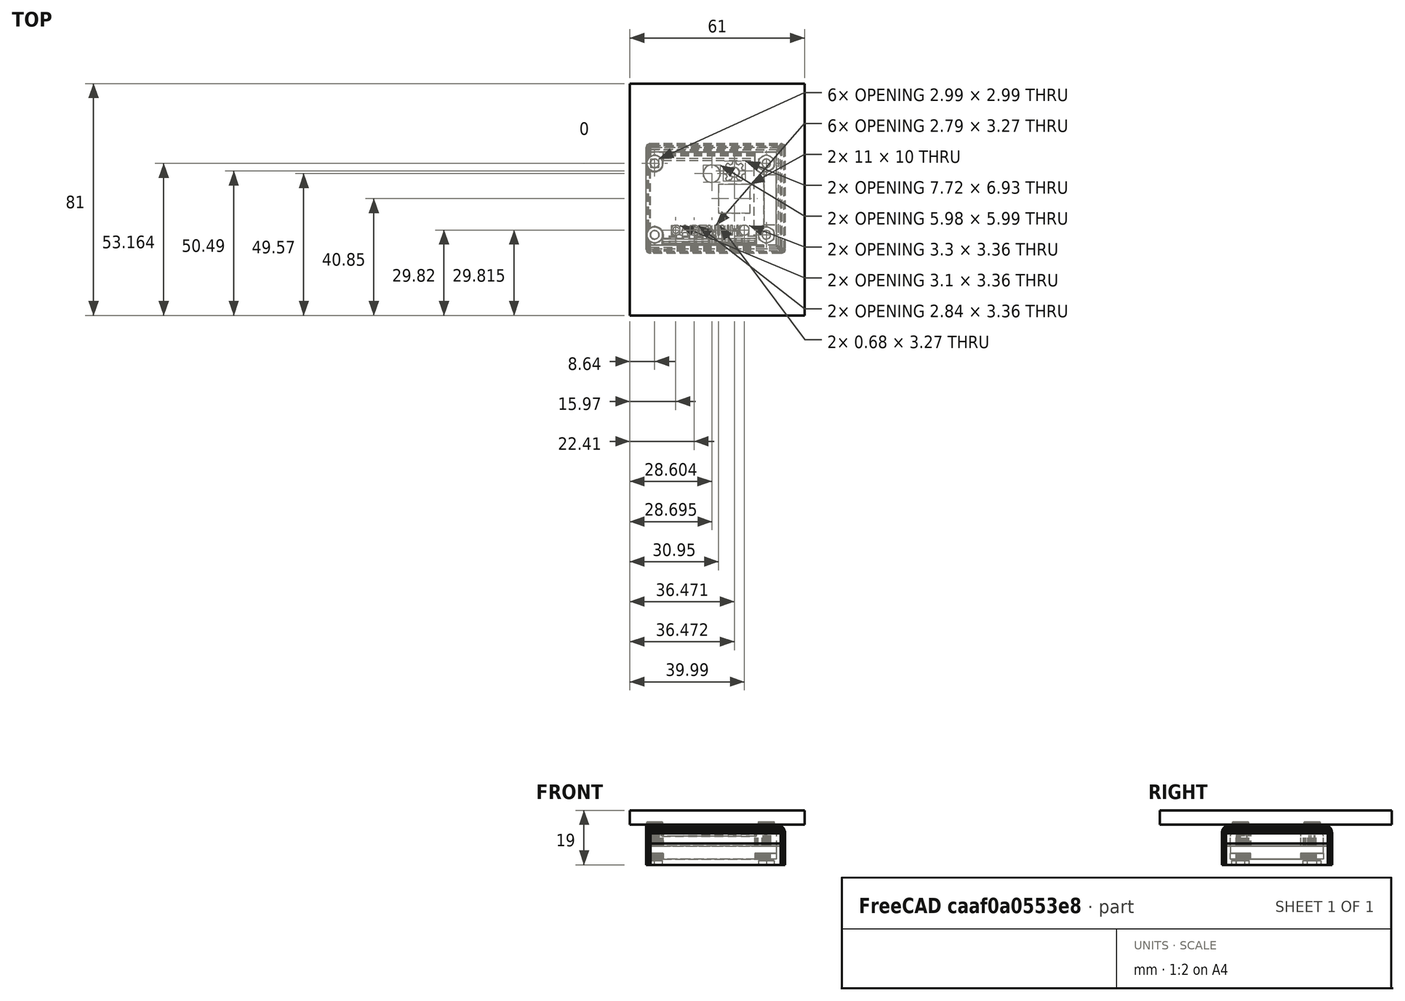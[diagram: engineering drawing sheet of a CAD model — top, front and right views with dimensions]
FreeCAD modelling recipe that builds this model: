
FCSTD DOCUMENT  (FreeCAD 0.15R4671 (Git))
Label: CASENINHO_V1
License: All rights reserved
LicenseURL: http://en.wikipedia.org/wiki/All_rights_reserved
objects: Part::Feature×6, Mesh::Feature×2, Part::Extrusion×2, Part::Part2DObjectPython×1, Part::Cut×1
note: 10 computed .brp shape members not serialized (recipe doc carries the construction recipe); baked Part::Feature solids carry a one-line shape summary decoded from their .brp

FEATURE [Mesh::Feature] CASENINHO_TAMPA  label="CASENINHO-TAMPA"
FEATURE [Part::Feature] CASENINHO_TAMPA001
  shape: bbox 48.5 x 38.5 x 8.5 mm, 6410 faces, 0 solids (baked)
FEATURE [Part::Feature] CASENINHO_TAMPA001_solid  label="CASENINHO_TAMPA001 (Solid)"
  shape: bbox 48.5 x 38.5 x 8.5 mm, 6410 faces (baked)
FEATURE [Part::Feature] CASENINHO_TAMPA001_solid001  label="CASENINHO_TAMPA001 (Solid)001"
  shape: bbox 48.5 x 38.5 x 8.5 mm, 2393 faces (baked)
FEATURE [Part::Feature] CASENINHO_TAMPA001_solid001001  label="CASENINHO_TAMPA001 (Solid)002"
  shape: bbox 48.5 x 38.5 x 8.5 mm, 2393 faces (baked)
FEATURE [Part::Part2DObjectPython] Rectangle  # Draft 2D object (typed FeaturePython)
  ChamferSize = 0
  FilletRadius = 0
  Height = -81
  Length = 61
  MakeFace = true
  Placement = pos=(-8.63765,52.8333,10) rot=(0,0,1;0rad)
FEATURE [Part::Extrusion] Extrude_Rectangle  label="Rectangle_Extrude"
  Base = -> Rectangle
  Dir = (0,0,5)
  Solid = true
FEATURE [Part::Extrusion] Extrude_Rectangle001  label="Rectangle_Extrude001"
  Base = -> Rectangle
  Dir = (0,0,5)
  Solid = true
FEATURE [Part::Cut] Cut
  Base = -> CASENINHO_TAMPA001_solid001
  Tool = -> Extrude_Rectangle
FEATURE [Mesh::Feature] CASENINHO_BASSE  label="CASENINHO-BASSE"
FEATURE [Part::Feature] CASENINHO_BASSE001
  shape: bbox 48.5 x 38.5 x 7.5 mm, 870 faces, 0 solids (baked)
FEATURE [Part::Feature] CASENINHO_BASSE001_solid  label="CASENINHO_BASSE001 (Solid)"
  shape: bbox 48.5 x 38.5 x 7.5 mm, 870 faces (baked)
